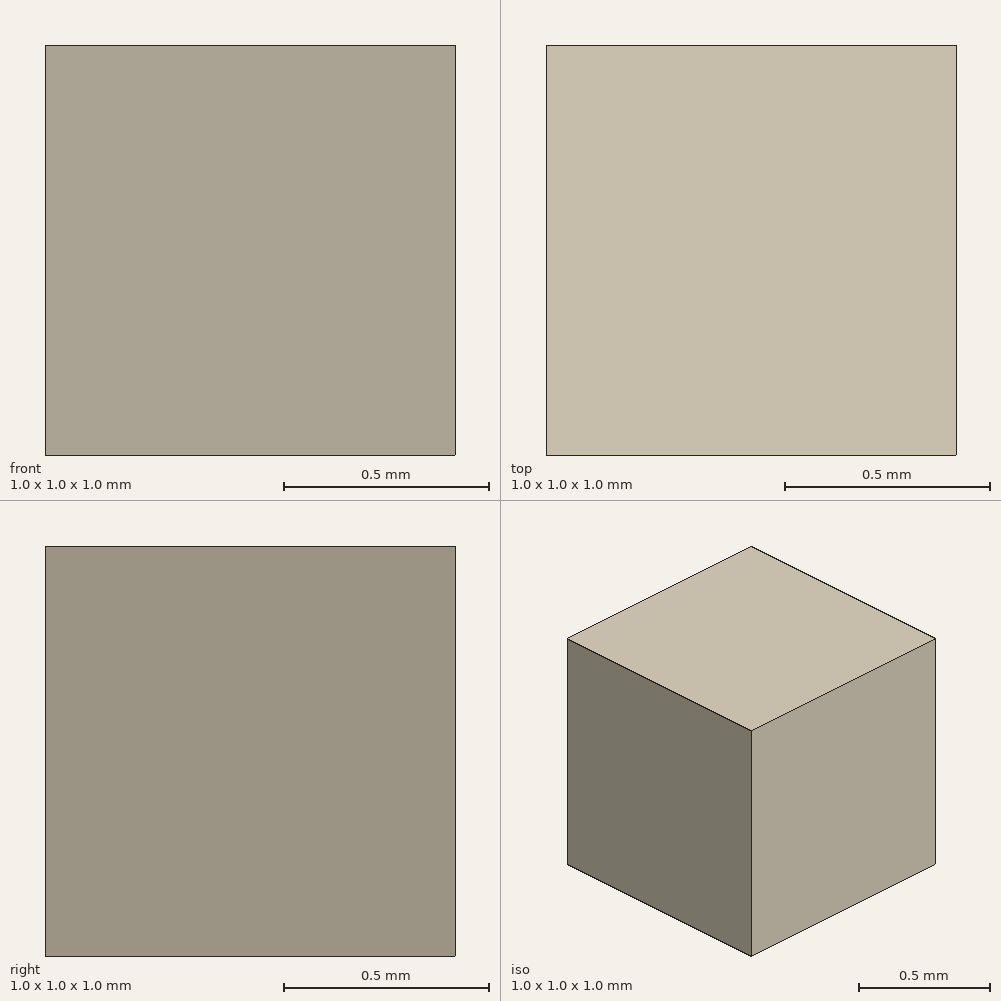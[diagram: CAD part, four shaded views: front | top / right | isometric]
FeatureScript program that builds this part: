
annotation { "Feature Type Name" : "Feature", "Feature Type Description" : "" }
export const myFeature = defineFeature(function(context is Context, id is Id, definition is map)
    precondition{}
    {
        {
            var Q0;
            Q0=qCreatedBy(makeId("Top.planeOp"),FACE);
            var sketch = newSketch(context, id + "F0", { "sketchPlane" : qUnion([Q0])});
            skLineSegment(sketch, "E0.bottom", {"start": v(-0.5, 0.5) * mm, "end": v(0.5, 0.5) * mm});
            skLineSegment(sketch, "E0.top", {"start": v(-0.5, -0.5) * mm, "end": v(0.5, -0.5) * mm});
            skLineSegment(sketch, "E0.left", {"start": v(-0.5, 0.5) * mm, "end": v(-0.5, -0.5) * mm});
            skLineSegment(sketch, "E0.right", {"start": v(0.5, 0.5) * mm, "end": v(0.5, -0.5) * mm});
            skSolve(sketch);
        }
        {
            var Q0;
            Q0 = qSketchRegion(id + "F0", true);
            extrude(context, id + "F1", {"entities" : qUnion([Q0]), "depth" : 1 * mm, "offsetDistance" : 25 * mm});
        }
    });
